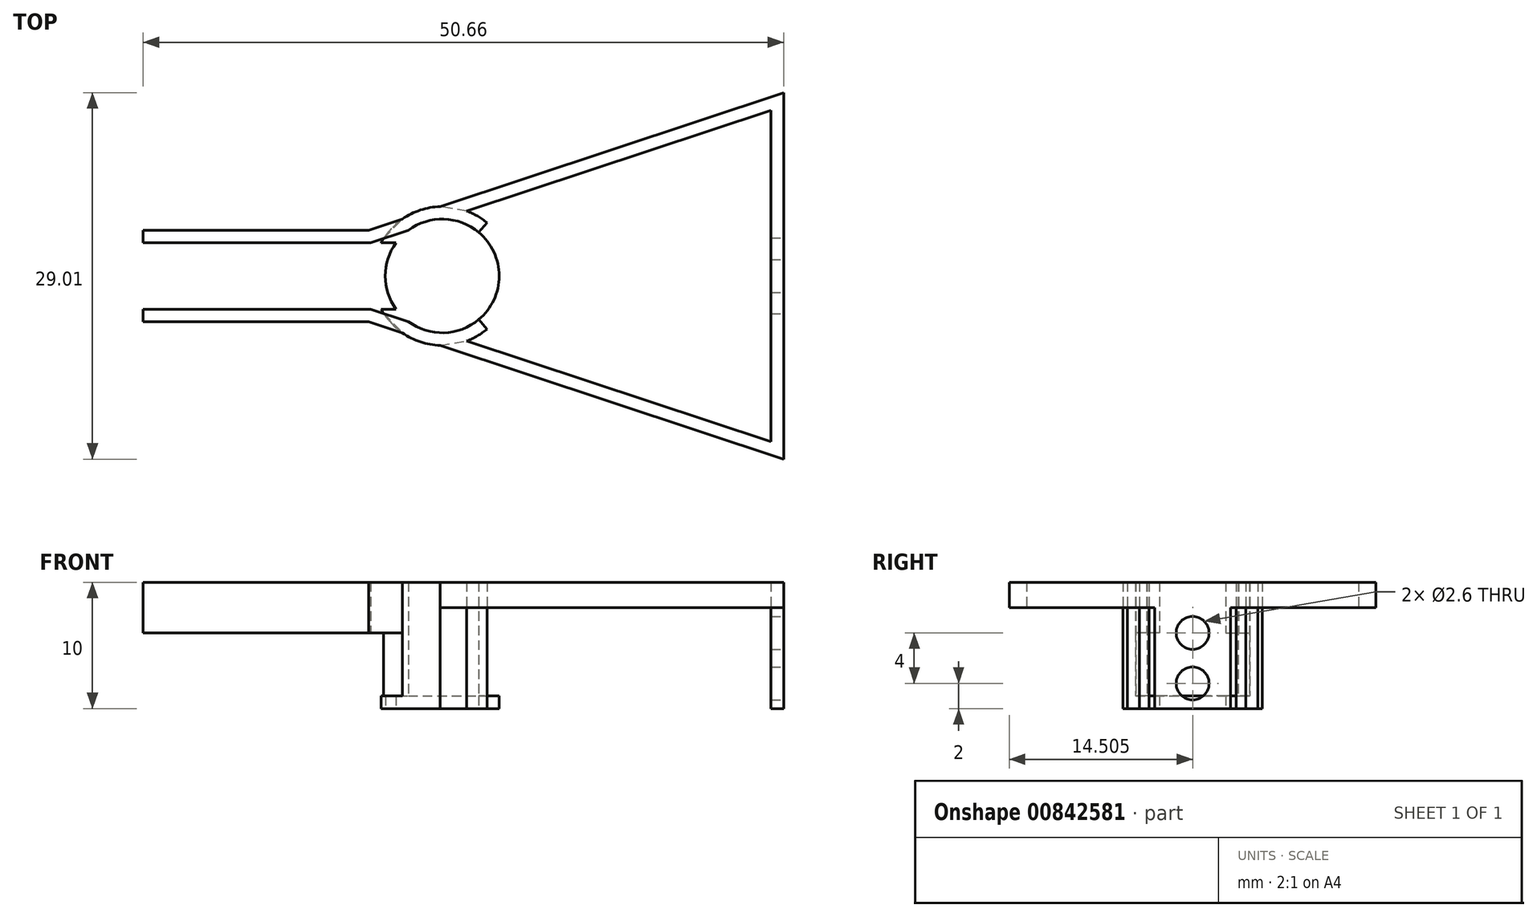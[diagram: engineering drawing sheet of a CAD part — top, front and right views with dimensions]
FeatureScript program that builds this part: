
annotation { "Feature Type Name" : "Feature", "Feature Type Description" : "" }
export const myFeature = defineFeature(function(context is Context, id is Id, definition is map)
    precondition{}
    {
        {
            var Q0;
            Q0=qCreatedBy(makeId("Top.planeOp"),FACE);
            var sketch = newSketch(context, id + "F0", { "sketchPlane" : qUnion([Q0])});
            skLineSegment(sketch, "E0.left", {"start": v(0, 0) * mm, "end": v(0, 5.25) * mm});
            skPoint(sketch, "E1", {"position": v(23.62, 2.62) * mm});
            skCircle(sketch, "E2", {"center": v(23.66, 2.62) * mm, "radius": 4.5 * mm});
            skPoint(sketch, "E3", {"position": v(20, 5.25) * mm});
            skPoint(sketch, "E4", {"position": v(20, 0) * mm});
            skPoint(sketch, "E5", {"position": v(18, 5.25) * mm});
            skPoint(sketch, "E6", {"position": v(18, 0) * mm});
            skLineSegment(sketch, "E7", {"start": v(23.66, 2.62) * mm, "end": v(23.66, 7.12) * mm});
            skLineSegment(sketch, "E8", {"start": v(23.66, 2.62) * mm, "end": v(23.66, -1.88) * mm});
            skLineSegment(sketch, "E9", {"start": v(0, 5.25) * mm, "end": v(20, 5.25) * mm});
            skLineSegment(sketch, "E10", {"start": v(0, 0) * mm, "end": v(20, 0) * mm});
            skLineSegment(sketch, "E11", {"start": v(18, 5.25) * mm, "end": v(23.66, 7.12) * mm});
            skLineSegment(sketch, "E12", {"start": v(23.66, 7.12) * mm, "end": v(49.66, 15.75) * mm});
            skLineSegment(sketch, "E13", {"start": v(18, 0) * mm, "end": v(23.66, -1.88) * mm});
            skLineSegment(sketch, "E14", {"start": v(23.66, -1.88) * mm, "end": v(49.66, -10.5) * mm});
            skLineSegment(sketch, "E15", {"start": v(49.66, 15.75) * mm, "end": v(49.66, -10.5) * mm});
            skPoint(sketch, "E16", {"position": v(0, 2.63) * mm});
            skLineSegment(sketch, "E17", {"start": v(23.66, 2.62) * mm, "end": v(49.66, 2.63) * mm});
            skLineSegment(sketch, "E18", {"start": v(23.66, 2.62) * mm, "end": v(49.66, 33.61) * mm});
            skLineSegment(sketch, "E19.MirrorCS", {"start": v(23.66, 2.62) * mm, "end": v(49.66, -28.36) * mm});
            skPoint(sketch, "E20", {"position": v(26.55, 6.07) * mm});
            skPoint(sketch, "E21", {"position": v(26.55, -0.82) * mm});
            skSolve(sketch);
        }
        {
            var Q0;
            Q0=qCreatedBy(makeId("Top.planeOp"),FACE);
            var sketch = newSketch(context, id + "F1", { "sketchPlane" : qUnion([Q0])});
            skCircle(sketch, "E22.0", {"center": v(23.66, 2.62) * mm, "radius": 5.5 * mm});
            skPoint(sketch, "E23", {"position": v(27.2, 6.84) * mm});
            skPoint(sketch, "E24", {"position": v(27.2, -1.59) * mm});
            skPoint(sketch, "E25", {"position": v(29.16, 2.63) * mm});
            skPoint(sketch, "E26", {"position": v(18.82, 5.25) * mm});
            skPoint(sketch, "E27", {"position": v(18.82, 0) * mm});
            skPoint(sketch, "E28", {"position": v(19.02, 5.59) * mm});
            skPoint(sketch, "E29", {"position": v(19.02, -0.34) * mm});
            skSolve(sketch);
        }
        {
            var Q0;
            Q0=makeQuery(id+"F1.imprint","IMPRINT",FACE,{"disambiguationData":[TD([[makeQuery(id+"F1.imprint","IMPRINT",EDGE,{"derivedFrom":sQuery(id+"F1.wireOp",EDGE,"E22.0")}),1.0]])]});
            extrude(context, id + "F2", {"entities" : qUnion([Q0]), "depth" : 10 * mm, "offsetDistance" : 25 * mm});
        }
        {
            var Q0;
            {var subQ0=sQuery(id+"F0.wireOp",EDGE,"E17");var subQ3=sQuery(id+"F0.wireOp",EDGE,"E2");var subQ4=makeQuery(id+"F0.imprint","INTERSECT",VERTEX,{"derivedFrom":[subQ3,subQ0]});Q0=makeQuery(id+"F0.imprint","IMPRINT",FACE,{"disambiguationData":[TD([[makeQuery(id+"F0.imprint","IMPRINT",EDGE,{"disambiguationData":[TD([[subQ4,1.0]])],"derivedFrom":subQ3}),-1.0]])]});}
            var Q1;
            {var subQ3=sQuery(id+"F0.wireOp",EDGE,"E2");var subQ7=sQuery(id+"F0.wireOp",EDGE,"E18");var subQ9=makeQuery(id+"F0.imprint","INTERSECT",VERTEX,{"derivedFrom":[subQ3,subQ7]});Q1=makeQuery(id+"F0.imprint","IMPRINT",FACE,{"disambiguationData":[TD([[makeQuery(id+"F0.imprint","IMPRINT",EDGE,{"disambiguationData":[TD([[subQ9,1.0]])],"derivedFrom":subQ3}),-1.0]])]});}
            var Q2;
            {var subQ0=sQuery(id+"F0.wireOp",EDGE,"E8");Q2=makeQuery(id+"F0.imprint","IMPRINT",FACE,{"disambiguationData":[TD([[makeQuery(id+"F0.imprint","IMPRINT",EDGE,{"derivedFrom":subQ0}),1.0]])]});}
            var Q3;
            {var subQ5=sQuery(id+"F0.wireOp",EDGE,"E7");Q3=makeQuery(id+"F0.imprint","IMPRINT",FACE,{"disambiguationData":[TD([[makeQuery(id+"F0.imprint","IMPRINT",EDGE,{"derivedFrom":subQ5}),1.0]])]});}
            var Q4;
            {var subQ0=sQuery(id+"F0.wireOp",EDGE,"E7");Q4=makeQuery(id+"F0.imprint","IMPRINT",FACE,{"disambiguationData":[TD([[makeQuery(id+"F0.imprint","IMPRINT",EDGE,{"derivedFrom":subQ0}),-1.0]])]});}
            var Q5;
            {var subQ0=sQuery(id+"F0.wireOp",EDGE,"E18");var subQ1=sQuery(id+"F0.wireOp",EDGE,"E2");var subQ2=makeQuery(id+"F0.imprint","INTERSECT",VERTEX,{"derivedFrom":[subQ1,subQ0]});Q5=makeQuery(id+"F0.imprint","IMPRINT",FACE,{"disambiguationData":[TD([[makeQuery(id+"F0.imprint","IMPRINT",EDGE,{"disambiguationData":[TD([[subQ2,1.0]])],"derivedFrom":subQ1}),1.0]])]});}
            var Q6;
            {var subQ0=sQuery(id+"F0.wireOp",EDGE,"E17");var subQ1=sQuery(id+"F0.wireOp",EDGE,"E2");var subQ2=makeQuery(id+"F0.imprint","INTERSECT",VERTEX,{"derivedFrom":[subQ1,subQ0]});Q6=makeQuery(id+"F0.imprint","IMPRINT",FACE,{"disambiguationData":[TD([[makeQuery(id+"F0.imprint","IMPRINT",EDGE,{"disambiguationData":[TD([[subQ2,1.0]])],"derivedFrom":subQ1}),1.0]])]});}
            var Q7;
            {var subQ0=sQuery(id+"F0.wireOp",EDGE,"E13");var subQ1=sQuery(id+"F0.wireOp",EDGE,"E2");var subQ3=makeQuery(id+"F0.imprint","INTERSECT",VERTEX,{"derivedFrom":[subQ1,subQ0]});Q7=makeQuery(id+"F0.imprint","IMPRINT",FACE,{"disambiguationData":[TD([[makeQuery(id+"F0.imprint","IMPRINT",EDGE,{"disambiguationData":[TD([[subQ3,-1.0]])],"derivedFrom":subQ1}),1.0]])]});}
            var Q8;
            {var subQ0=sQuery(id+"F0.wireOp",EDGE,"E11");var subQ1=sQuery(id+"F0.wireOp",EDGE,"E2");var subQ3=makeQuery(id+"F0.imprint","INTERSECT",VERTEX,{"derivedFrom":[subQ1,subQ0]});Q8=makeQuery(id+"F0.imprint","IMPRINT",FACE,{"disambiguationData":[TD([[makeQuery(id+"F0.imprint","IMPRINT",EDGE,{"disambiguationData":[TD([[subQ3,1.0]])],"derivedFrom":subQ1}),1.0]])]});}
            extrude(context, id + "F3", {"entities" : qUnion([Q0, Q1, Q2, Q3, Q4, Q5, Q6, Q7, Q8]), "operationType" : NewBodyOperationType.REMOVE, "depth" : 10 * mm, "offsetDistance" : 25 * mm});
        }
        {
            var Q0;
            Q0=qCreatedBy(makeId("Top.planeOp"),FACE);
            var sketch = newSketch(context, id + "F4", { "sketchPlane" : qUnion([Q0])});
            skLineSegment(sketch, "E30", {"start": v(18, 5.25) * mm, "end": v(19.02, 5.59) * mm});
            skLineSegment(sketch, "E31", {"start": v(18, 5.25) * mm, "end": v(0, 5.25) * mm});
            skLineSegment(sketch, "E32.MirrorCS", {"start": v(18, 0) * mm, "end": v(19.02, -0.34) * mm});
            skLineSegment(sketch, "E33.MirrorCS", {"start": v(18, 0) * mm, "end": v(0, 0) * mm});
            skLineSegment(sketch, "E34.0", {"start": v(17.84, 6.25) * mm, "end": v(20.5, 7.13) * mm});
            skLineSegment(sketch, "E34.1", {"start": v(17.84, -1) * mm, "end": v(20.5, -1.88) * mm});
            skLineSegment(sketch, "E35", {"start": v(19.02, 5.59) * mm, "end": v(20.5, 7.13) * mm});
            skLineSegment(sketch, "E36", {"start": v(19.02, -0.34) * mm, "end": v(20.5, -1.88) * mm});
            skLineSegment(sketch, "E37", {"start": v(0, 5.25) * mm, "end": v(0, 6.25) * mm});
            skLineSegment(sketch, "E38", {"start": v(0, 0) * mm, "end": v(0, -1) * mm});
            skLineSegment(sketch, "E39", {"start": v(0, 6.25) * mm, "end": v(17.84, 6.25) * mm});
            skLineSegment(sketch, "E40", {"start": v(0, -1) * mm, "end": v(17.84, -1) * mm});
            skSolve(sketch);
        }
        {
            var Q0;
            Q0=makeQuery(id+"F4.imprint","IMPRINT",FACE,{"disambiguationData":[TD([[makeQuery(id+"F4.imprint","IMPRINT",EDGE,{"derivedFrom":sQuery(id+"F4.wireOp",EDGE,"E30")}),1.0]])]});
            var Q1;
            Q1=makeQuery(id+"F4.imprint","IMPRINT",FACE,{"disambiguationData":[TD([[makeQuery(id+"F4.imprint","IMPRINT",EDGE,{"derivedFrom":sQuery(id+"F4.wireOp",EDGE,"E32.MirrorCS")}),-1.0]])]});
            extrude(context, id + "F5", {"entities" : qUnion([Q0, Q1]), "operationType" : NewBodyOperationType.ADD, "depth" : 10 * mm, "offsetDistance" : 25 * mm});
        }
        {
            var Q0;
            Q0 = qSketchRegion(id + "F4", true);
            extrude(context, id + "F6", {"entities" : qUnion([Q0]), "operationType" : NewBodyOperationType.REMOVE, "depth" : 6 * mm, "offsetDistance" : 25 * mm});
        }
        {
            var Q0;
            {var subQ4=sQuery(id+"F0.wireOp",EDGE,"E0.left");Q0=makeQuery(id+"F0.imprint","IMPRINT",FACE,{"disambiguationData":[TD([[makeQuery(id+"F0.imprint","IMPRINT",EDGE,{"derivedFrom":subQ4}),-1.0]])]});}
            var Q1;
            {var subQ0=sQuery(id+"F0.wireOp",EDGE,"E10");var subQ1=sQuery(id+"F0.wireOp",EDGE,"E2");var subQ2=makeQuery(id+"F0.imprint","INTERSECT",VERTEX,{"derivedFrom":[subQ1,subQ0]});Q1=makeQuery(id+"F0.imprint","IMPRINT",FACE,{"disambiguationData":[TD([[makeQuery(id+"F0.imprint","IMPRINT",EDGE,{"disambiguationData":[TD([[subQ2,-1.0]])],"derivedFrom":subQ1}),-1.0]])]});}
            var Q2;
            {var subQ0=sQuery(id+"F0.wireOp",EDGE,"E9");var subQ1=sQuery(id+"F0.wireOp",EDGE,"E2");var subQ2=makeQuery(id+"F0.imprint","INTERSECT",VERTEX,{"derivedFrom":[subQ1,subQ0]});Q2=makeQuery(id+"F0.imprint","IMPRINT",FACE,{"disambiguationData":[TD([[makeQuery(id+"F0.imprint","IMPRINT",EDGE,{"disambiguationData":[TD([[subQ2,1.0]])],"derivedFrom":subQ1}),-1.0]])]});}
            extrude(context, id + "F7", {"entities" : qUnion([Q0, Q1, Q2]), "operationType" : NewBodyOperationType.REMOVE, "depth" : 10 * mm, "offsetDistance" : 25 * mm});
        }
        {
            var Q0;
            Q0=makeQuery(id+"F1.imprint","IMPRINT",FACE,{"disambiguationData":[TD([[makeQuery(id+"F1.imprint","IMPRINT",EDGE,{"derivedFrom":sQuery(id+"F1.wireOp",EDGE,"E22.0")}),1.0]])]});
            extrude(context, id + "F8", {"entities" : qUnion([Q0]), "operationType" : NewBodyOperationType.ADD, "depth" : 1 * mm, "offsetDistance" : 25 * mm});
        }
        {
            var Q0;
            {var subQ4=sQuery(id+"F0.wireOp",EDGE,"E0.left");Q0=makeQuery(id+"F0.imprint","IMPRINT",FACE,{"disambiguationData":[TD([[makeQuery(id+"F0.imprint","IMPRINT",EDGE,{"derivedFrom":subQ4}),-1.0]])]});}
            var Q1;
            {var subQ0=sQuery(id+"F0.wireOp",EDGE,"E17");var subQ3=sQuery(id+"F0.wireOp",EDGE,"E2");var subQ4=makeQuery(id+"F0.imprint","INTERSECT",VERTEX,{"derivedFrom":[subQ3,subQ0]});Q1=makeQuery(id+"F0.imprint","IMPRINT",FACE,{"disambiguationData":[TD([[makeQuery(id+"F0.imprint","IMPRINT",EDGE,{"disambiguationData":[TD([[subQ4,1.0]])],"derivedFrom":subQ3}),-1.0]])]});}
            var Q2;
            {var subQ3=sQuery(id+"F0.wireOp",EDGE,"E2");var subQ7=sQuery(id+"F0.wireOp",EDGE,"E18");var subQ9=makeQuery(id+"F0.imprint","INTERSECT",VERTEX,{"derivedFrom":[subQ3,subQ7]});Q2=makeQuery(id+"F0.imprint","IMPRINT",FACE,{"disambiguationData":[TD([[makeQuery(id+"F0.imprint","IMPRINT",EDGE,{"disambiguationData":[TD([[subQ9,1.0]])],"derivedFrom":subQ3}),-1.0]])]});}
            extrude(context, id + "F9", {"entities" : qUnion([Q0, Q1, Q2]), "operationType" : NewBodyOperationType.REMOVE, "depth" : 1 * mm, "offsetDistance" : 25 * mm});
        }
        {
            var Q0;
            Q0=qCreatedBy(makeId("Top.planeOp"),FACE);
            var sketch = newSketch(context, id + "F10", { "sketchPlane" : qUnion([Q0])});
            skPoint(sketch, "E41", {"position": v(25.6, 7.77) * mm});
            skLineSegment(sketch, "E42", {"start": v(25.6, 7.77) * mm, "end": v(49.66, 15.75) * mm});
            skLineSegment(sketch, "E43.MirrorCS", {"start": v(25.6, -2.52) * mm, "end": v(49.66, -10.5) * mm});
            skPoint(sketch, "E44.MirrorP", {"position": v(25.6, -2.52) * mm});
            skLineSegment(sketch, "E45", {"start": v(49.66, 15.75) * mm, "end": v(49.66, -10.5) * mm});
            skLineSegment(sketch, "E46.0", {"start": v(23.49, -2.87) * mm, "end": v(50.66, -11.88) * mm});
            skLineSegment(sketch, "E46.1", {"start": v(50.66, 17.13) * mm, "end": v(50.66, -11.88) * mm});
            skLineSegment(sketch, "E46.2", {"start": v(23.49, 8.12) * mm, "end": v(50.66, 17.13) * mm});
            skLineSegment(sketch, "E47", {"start": v(23.49, -2.87) * mm, "end": v(25.6, -2.52) * mm});
            skLineSegment(sketch, "E48", {"start": v(25.6, 7.77) * mm, "end": v(23.49, 8.12) * mm});
            skPoint(sketch, "E49", {"position": v(49.66, 2.63) * mm});
            skLineSegment(sketch, "E50", {"start": v(49.66, 2.62) * mm, "end": v(50.66, 2.62) * mm});
            skLineSegment(sketch, "E51", {"start": v(49.66, 5.63) * mm, "end": v(50.66, 5.63) * mm});
            skLineSegment(sketch, "E52.MirrorCS", {"start": v(49.66, -0.37) * mm, "end": v(50.66, -0.37) * mm});
            skSolve(sketch);
        }
        {
            var Q0;
            {var subQ1=sQuery(id+"F10.wireOp",EDGE,"E42");Q0=makeQuery(id+"F10.imprint","IMPRINT",FACE,{"disambiguationData":[TD([[makeQuery(id+"F10.imprint","IMPRINT",EDGE,{"derivedFrom":subQ1}),1.0]])]});}
            var Q1;
            {var subQ4=sQuery(id+"F10.wireOp",EDGE,"E43.MirrorCS");Q1=makeQuery(id+"F10.imprint","IMPRINT",FACE,{"disambiguationData":[TD([[makeQuery(id+"F10.imprint","IMPRINT",EDGE,{"derivedFrom":subQ4}),-1.0]])]});}
            var Q2;
            {var subQ0=sQuery(id+"F10.wireOp",EDGE,"E50");Q2=makeQuery(id+"F10.imprint","IMPRINT",FACE,{"disambiguationData":[TD([[makeQuery(id+"F10.imprint","IMPRINT",EDGE,{"derivedFrom":subQ0}),-1.0]])]});}
            var Q3;
            {var subQ0=sQuery(id+"F10.wireOp",EDGE,"E50");Q3=makeQuery(id+"F10.imprint","IMPRINT",FACE,{"disambiguationData":[TD([[makeQuery(id+"F10.imprint","IMPRINT",EDGE,{"derivedFrom":subQ0}),1.0]])]});}
            extrude(context, id + "F11", {"entities" : qUnion([Q0, Q1, Q2, Q3]), "operationType" : NewBodyOperationType.ADD, "depth" : 10 * mm, "offsetDistance" : 25 * mm});
        }
        {
            var Q0;
            {var subQ1=sQuery(id+"F10.wireOp",EDGE,"E42");Q0=makeQuery(id+"F10.imprint","IMPRINT",FACE,{"disambiguationData":[TD([[makeQuery(id+"F10.imprint","IMPRINT",EDGE,{"derivedFrom":subQ1}),1.0]])]});}
            var Q1;
            {var subQ4=sQuery(id+"F10.wireOp",EDGE,"E43.MirrorCS");Q1=makeQuery(id+"F10.imprint","IMPRINT",FACE,{"disambiguationData":[TD([[makeQuery(id+"F10.imprint","IMPRINT",EDGE,{"derivedFrom":subQ4}),-1.0]])]});}
            extrude(context, id + "F12", {"entities" : qUnion([Q0, Q1]), "operationType" : NewBodyOperationType.REMOVE, "depth" : 8 * mm, "offsetDistance" : 25 * mm});
        }
        {
            var Q0;
            Q0=makeQuery(id+"F11.opExtrude","SWEPT_FACE",FACE,{"disambiguationData":[OSD([sQuery(id+"F10.wireOp",EDGE,"E46.1")])]});
            var sketch = newSketch(context, id + "F13", { "sketchPlane" : qUnion([Q0])});
            skLineSegment(sketch, "E53", {"start": v(-0.38, 8) * mm, "end": v(-0.38, 10) * mm});
            skLineSegment(sketch, "E54", {"start": v(5.62, 8) * mm, "end": v(5.62, 10) * mm});
            skPoint(sketch, "E55", {"position": v(2.62, 4) * mm});
            skPoint(sketch, "E56", {"position": v(2.62, 6) * mm});
            skCircle(sketch, "E57", {"center": v(2.62, 6) * mm, "radius": 1.3 * mm});
            skLineSegment(sketch, "E58", {"start": v(2.62, 4) * mm, "end": v(-0.38, 4) * mm});
            skLineSegment(sketch, "E59", {"start": v(2.62, 4) * mm, "end": v(5.62, 4) * mm});
            skPoint(sketch, "E60.MirrorP", {"position": v(2.62, 2) * mm});
            skCircle(sketch, "E61.MirrorC", {"center": v(2.62, 2) * mm, "radius": 1.3 * mm});
            skLineSegment(sketch, "E62", {"start": v(-0.38, 8) * mm, "end": v(5.62, 8) * mm});
            skPoint(sketch, "E63", {"position": v(2.62, 8) * mm});
            skLineSegment(sketch, "E64", {"start": v(2.62, 8) * mm, "end": v(2.62, 0) * mm});
            skSolve(sketch);
        }
        {
            var Q0;
            Q0 = qSketchRegion(id + "F13", true);
            extrude(context, id + "F14", {"entities" : qUnion([Q0]), "operationType" : NewBodyOperationType.REMOVE, "oppositeDirection" : true, "depth" : 1 * mm, "offsetDistance" : 25 * mm});
        }
    });
